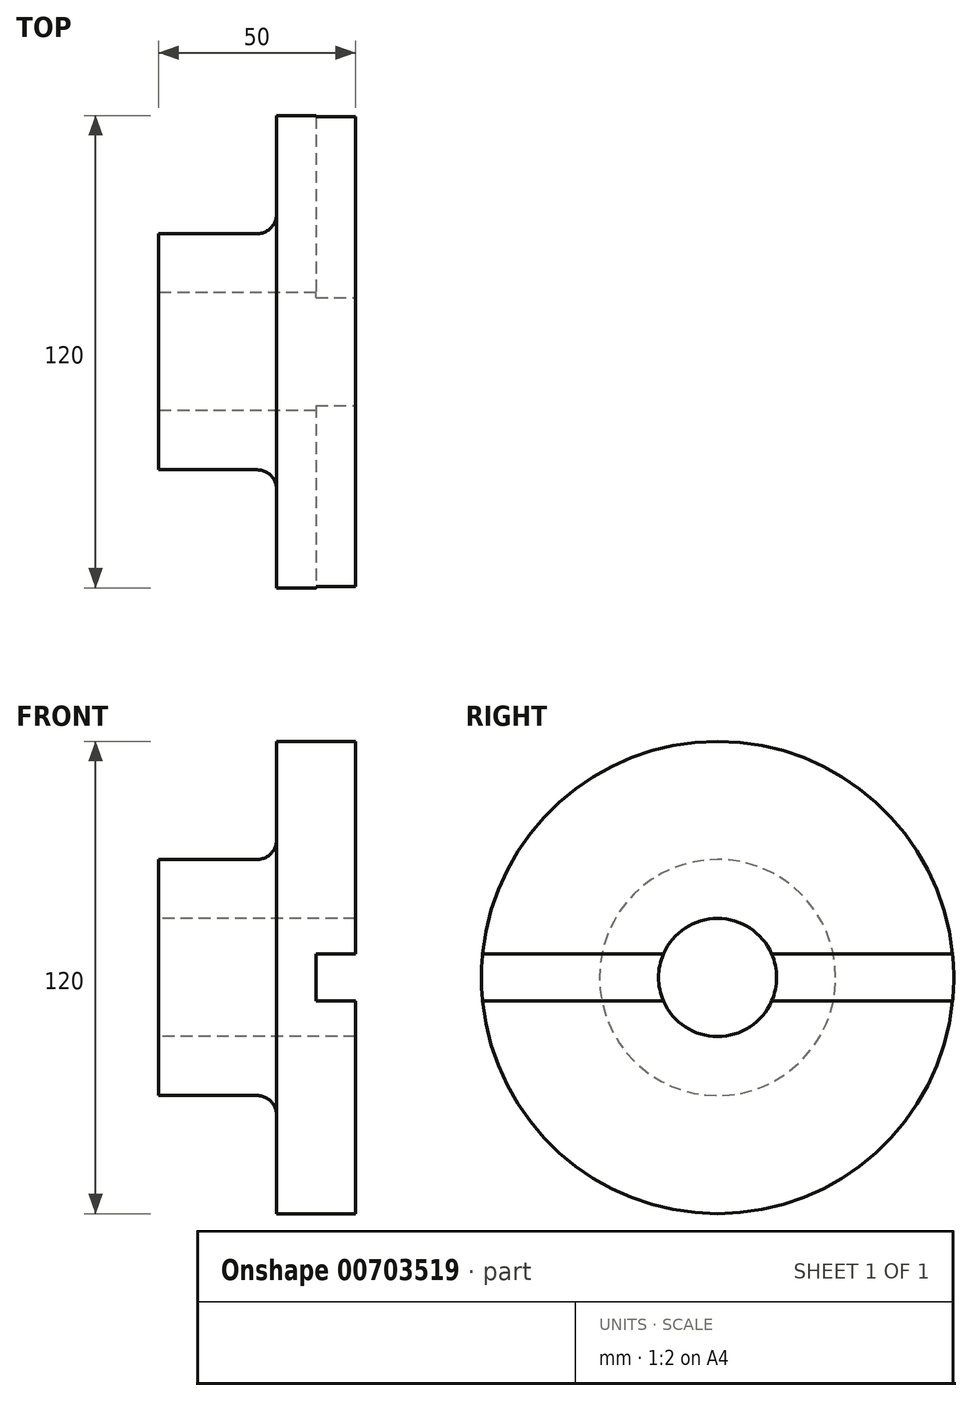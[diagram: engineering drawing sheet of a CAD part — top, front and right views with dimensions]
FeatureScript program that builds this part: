
annotation { "Feature Type Name" : "Feature", "Feature Type Description" : "" }
export const myFeature = defineFeature(function(context is Context, id is Id, definition is map)
    precondition{}
    {
        {
            var Q0;
            Q0=qCreatedBy(makeId("Top.planeOp"),FACE);
            var sketch = newSketch(context, id + "F0", { "sketchPlane" : qUnion([Q0])});
            skLineSegment(sketch, "E0", {"start": v(0, 0) * mm, "end": v(0, 6) * mm});
            skLineSegment(sketch, "E1", {"start": v(0, 6) * mm, "end": v(-10, 6) * mm});
            skLineSegment(sketch, "E2", {"start": v(-10, 6) * mm, "end": v(-10, 0) * mm});
            skLineSegment(sketch, "E3", {"start": v(-10, 0) * mm, "end": v(0, 0) * mm});
            skLineSegment(sketch, "E4", {"start": v(0, 6) * mm, "end": v(0, 60) * mm});
            skLineSegment(sketch, "E5", {"start": v(0, 60) * mm, "end": v(-20, 60) * mm});
            skLineSegment(sketch, "E6", {"start": v(-20, 60) * mm, "end": v(-20, 35) * mm});
            skLineSegment(sketch, "E7", {"start": v(-25, 30) * mm, "end": v(-50, 30) * mm});
            skLineSegment(sketch, "E8", {"start": v(-50, 30) * mm, "end": v(-50, 0) * mm});
            skLineSegment(sketch, "E9", {"start": v(-50, 0) * mm, "end": v(0, 0) * mm});
            skLineSegment(sketch, "E10", {"start": v(-50, 30) * mm, "end": v(-50, 15) * mm});
            skLineSegment(sketch, "E11", {"start": v(-50, 15) * mm, "end": v(0, 15) * mm});
            skPoint(sketch, "E12.visualSharp", {"position": v(-20, 30) * mm});
            skArc(sketch, "E12.filletArc", {"start": v(-25, 30) * mm, "mid": v(-21.46, 31.46) * mm, "end": v(-20, 35) * mm});
            skSolve(sketch);
        }
        {
            var Q0;
            {var subQ0=sQuery(id+"F0.wireOp",EDGE,"E5");Q0=makeQuery(id+"F0.imprint","IMPRINT",FACE,{"disambiguationData":[TD([[makeQuery(id+"F0.imprint","IMPRINT",EDGE,{"derivedFrom":subQ0}),1.0]])]});}
            var Q1;
            Q1=sQuery(id+"F0.wireOp",EDGE,"E9");
            revolve(context, id + "F1", {"surfaceOperationType" : NewSurfaceOperationType.NEW, "entities" : qUnion([Q0]), "axis" : qUnion([Q1]), "revolveType" : RevolveType.FULL});
        }
        {
            var Q0;
            Q0=makeQuery(id+"F1.opRevolve","SWEPT_FACE",FACE,{"disambiguationData":[OSD([sQuery(id+"F0.wireOp",EDGE,"E4")])]});
            var sketch = newSketch(context, id + "F2", { "sketchPlane" : qUnion([Q0])});
            skLineSegment(sketch, "E13", {"start": v(60, 0) * mm, "end": v(60, -6) * mm});
            skLineSegment(sketch, "E14", {"start": v(60, 0) * mm, "end": v(60, 6) * mm});
            skLineSegment(sketch, "E15", {"start": v(60, -6) * mm, "end": v(-64.51, -6) * mm});
            skLineSegment(sketch, "E16", {"start": v(-64.51, -6) * mm, "end": v(-64.51, 6) * mm});
            skLineSegment(sketch, "E17", {"start": v(-64.51, 6) * mm, "end": v(60, 6) * mm});
            skSolve(sketch);
        }
        {
            var Q0;
            {var subQ0=sQuery(id+"F2.wireOp",EDGE,"E15");var subQ1=sQuery(id+"F0.wireOp",EDGE,"E4");var subQ2=makeQuery(id+"F1.opRevolve","SWEPT_EDGE",EDGE,{"disambiguationData":[OSD([subQ1,sQuery(id+"F0.wireOp",EDGE,"E5")])]});var subQ3=makeQuery(id+"F2.imprint","INTERSECT",VERTEX,{"disambiguationData":[OD(1.0)],"derivedFrom":[subQ2,subQ0]});Q0=makeQuery(id+"F2.imprint","IMPRINT",FACE,{"disambiguationData":[TD([[makeQuery(id+"F2.imprint","IMPRINT",EDGE,{"disambiguationData":[TD([[subQ3,1.0]])],"derivedFrom":subQ0}),-1.0]])]});}
            var Q1;
            {var subQ0=sQuery(id+"F2.wireOp",EDGE,"E16");Q1=makeQuery(id+"F2.imprint","IMPRINT",FACE,{"disambiguationData":[TD([[makeQuery(id+"F2.imprint","IMPRINT",EDGE,{"derivedFrom":subQ0}),-1.0]])]});}
            var Q2;
            {var subQ0=sQuery(id+"F0.wireOp",EDGE,"E4");var subQ1=makeQuery(id+"F1.opRevolve","SWEPT_EDGE",EDGE,{"disambiguationData":[OSD([subQ0,sQuery(id+"F0.wireOp",EDGE,"E5")])]});var subQ5=sQuery(id+"F2.wireOp",EDGE,"E15");var subQ6=makeQuery(id+"F2.imprint","INTERSECT",VERTEX,{"disambiguationData":[OD(0.0)],"derivedFrom":[subQ1,subQ5]});Q2=makeQuery(id+"F2.imprint","IMPRINT",FACE,{"disambiguationData":[TD([[makeQuery(id+"F2.imprint","IMPRINT",EDGE,{"disambiguationData":[TD([[subQ6,-1.0]])],"derivedFrom":subQ5}),-1.0]])]});}
            extrude(context, id + "F3", {"entities" : qUnion([Q0, Q1, Q2]), "operationType" : NewBodyOperationType.REMOVE, "oppositeDirection" : true, "depth" : 10 * mm, "offsetDistance" : 25 * mm});
        }
    });
